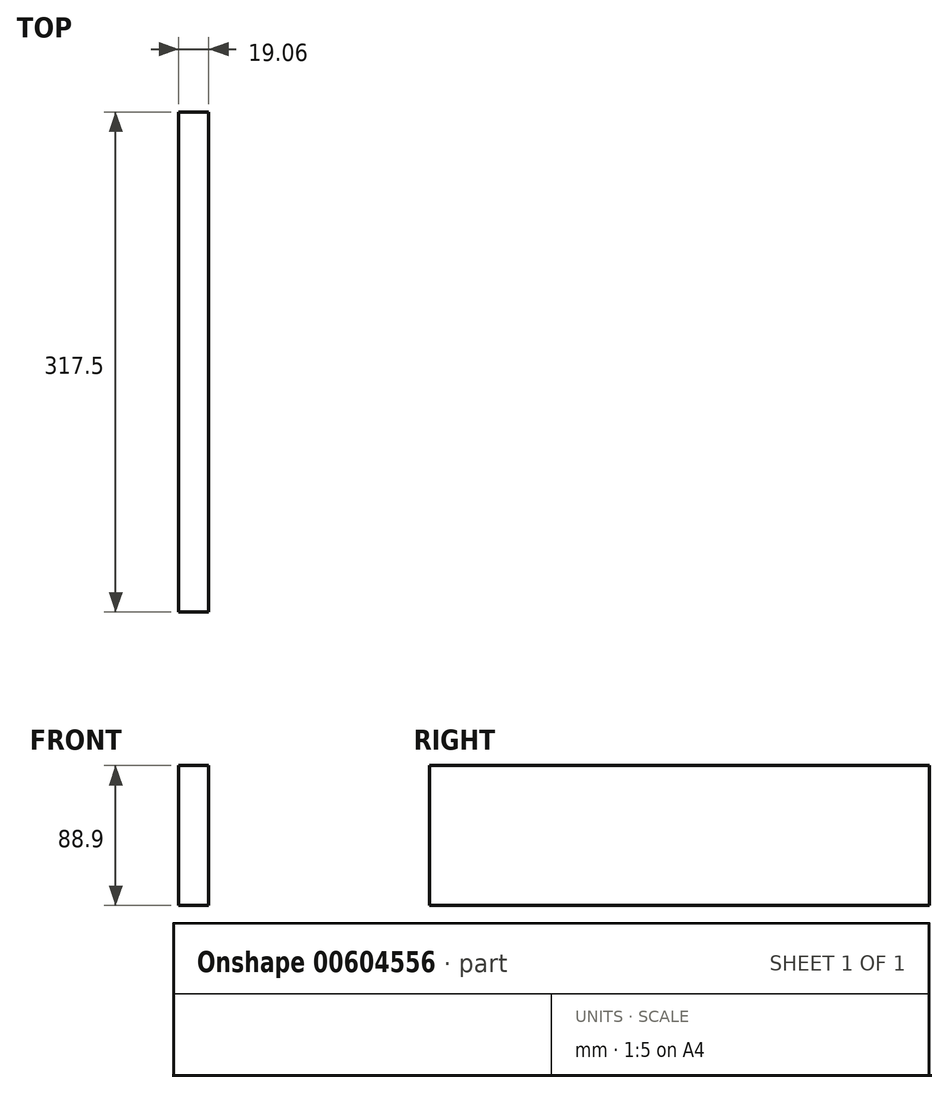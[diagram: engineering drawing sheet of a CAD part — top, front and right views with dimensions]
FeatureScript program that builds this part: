
annotation { "Feature Type Name" : "Feature", "Feature Type Description" : "" }
export const myFeature = defineFeature(function(context is Context, id is Id, definition is map)
    precondition{}
    {
        {
            var Q0;
            Q0=qCreatedBy(makeId("Front.planeOp"),FACE);
            var sketch = newSketch(context, id + "F0", { "sketchPlane" : qUnion([Q0])});
            skLineSegment(sketch, "E0.bottom", {"start": v(9.53, 44.45) * mm, "end": v(-9.52, 44.45) * mm});
            skLineSegment(sketch, "E0.top", {"start": v(9.52, -44.45) * mm, "end": v(-9.53, -44.45) * mm});
            skLineSegment(sketch, "E0.left", {"start": v(9.53, 44.45) * mm, "end": v(9.52, -44.45) * mm});
            skLineSegment(sketch, "E0.right", {"start": v(-9.52, 44.45) * mm, "end": v(-9.53, -44.45) * mm});
            skPoint(sketch, "E0.middle", {"position": v(0, 0) * mm});
            skSolve(sketch);
        }
        {
            var Q0;
            Q0=makeQuery(id+"F0.imprint","IMPRINT",FACE,{"disambiguationData":[TD([[makeQuery(id+"F0.imprint","IMPRINT",EDGE,{"derivedFrom":sQuery(id+"F0.wireOp",EDGE,"E0.bottom")}),1.0]])]});
            extrude(context, id + "F1", {"entities" : qUnion([Q0]), "depth" : 317.5 * mm});
        }
    });
